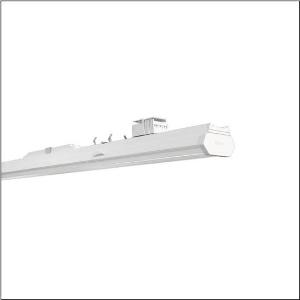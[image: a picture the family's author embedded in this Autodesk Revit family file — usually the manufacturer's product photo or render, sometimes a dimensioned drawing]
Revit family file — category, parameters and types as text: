
# Revit family: licross_r__21_protected_ho_52td1bcn4b5m_1c3e
name_source: partatom
category: Lighting Fixtures
units: mm (PartAtom-declared; Revit-internal decimal feet)

## family parameters
Cut with Voids When Loaded = No
Host = Face
Light Source = No
Part Type = Normal
Room Calculation Point = No
Round Connector Dimension = Use Diameter
Shared = No

## types (1)
- --- (1 x LED, 11820 lm, 68.9 W, 4000K)
    Apparent Load = 69 VA
    CIE Flux Codes = 54 82 95 97 100
    Color Rendering = 80
    Color Temperature = 4000K
    Default Elevation = 1800 mm
    Description = Licross® 21 Protected HO, luminaire insert, of sheet steel, galvanised, coil coated, white, length: 1.500mm, width: 90mm, height: 103mm, LED rated luminous flux: 11.830lm, light colour: 840, SDCM (Standard Deviation of Colour Matching)MacAdam ≤ 3 SDCM (initial), control gear: ON/OFF Multilumen, CLOi, with plug, 3-pole, with phase selection, mains connection: 220..240V, AC, 50/60Hz, start of lifetime: 69W, end of service life: 83W, internal wiring halogen-free, primary optical cover: cover, of PMMA, light emission: direct distribution, primary light characteristic: symmetric, protection rating (complete): IP54, insulation class (complete): insulation class I (protective earthing), certification: CE, ENEC, VDE, UKCA, protection symbol: D if used in an environment with non-conductive dust loads with corresponding accessories, impact resistance: IK06, permissible ambient temperature for indoor applications: -35..+35°C, corresponds to IFS (International Featured Standards) requirements for safety and quality in the food industry, reducing of maximum allowable ambient temperature of 5°C with ceiling mounting, LABS conformity tested according to VDMA 24364:2018-05, packaging unit: 1 piece
    Height = 92 mm
    Lamp = 1 x LED
    Lamp Light Flux = 11820 lm
    Lamp Power = 68.9 W
    Lamp count = 1
    Length = 1500 mm
    Luminous efficacy = 172 lm/W
    Manufacturer = Siteco
    ModVariant = No
    Model = 52TD1BCN4B5M
    Mounting Place = Ceiling
    Mounting Type = Pendant
    Number of Poles = 1
    OnlyDefault = Yes
    Power Factor = 1
    Product Name = Licross® 21 Protected HO
    Product group = luminaire insert | ceiling pendant
    ProductGroupID = 901
    Protection Class = Protection class I
    Protection Degree = IP 54
    RLX_Detail_Level = 1
    RLX_Emergency_Light_Flux = 0 lm
    RLX_Emergency_Type = 0
    RLX_Emergency_Type_DB = No
    RlxData = <blob elided: 22113 chars, md5=31415810>
    Socket = socket
    Standby Power = 0 W
    System Light Flux = 11820 lm
    System Power = 69 W
    Type Comments = factory setting: luminous flux: 100 % | (A | C | E) | 162 mA
    Type Image = l_1256148.jpg
    URL = http://relux.com
    VarID = @adj_115439
    Voltage = 0 V
    Weight = 0.00 kg
    Width = 88 mm

## geometry (parser evidence)
native form markers: Blend x4, Sweep x12
no freeform markers — native parametric forms only
